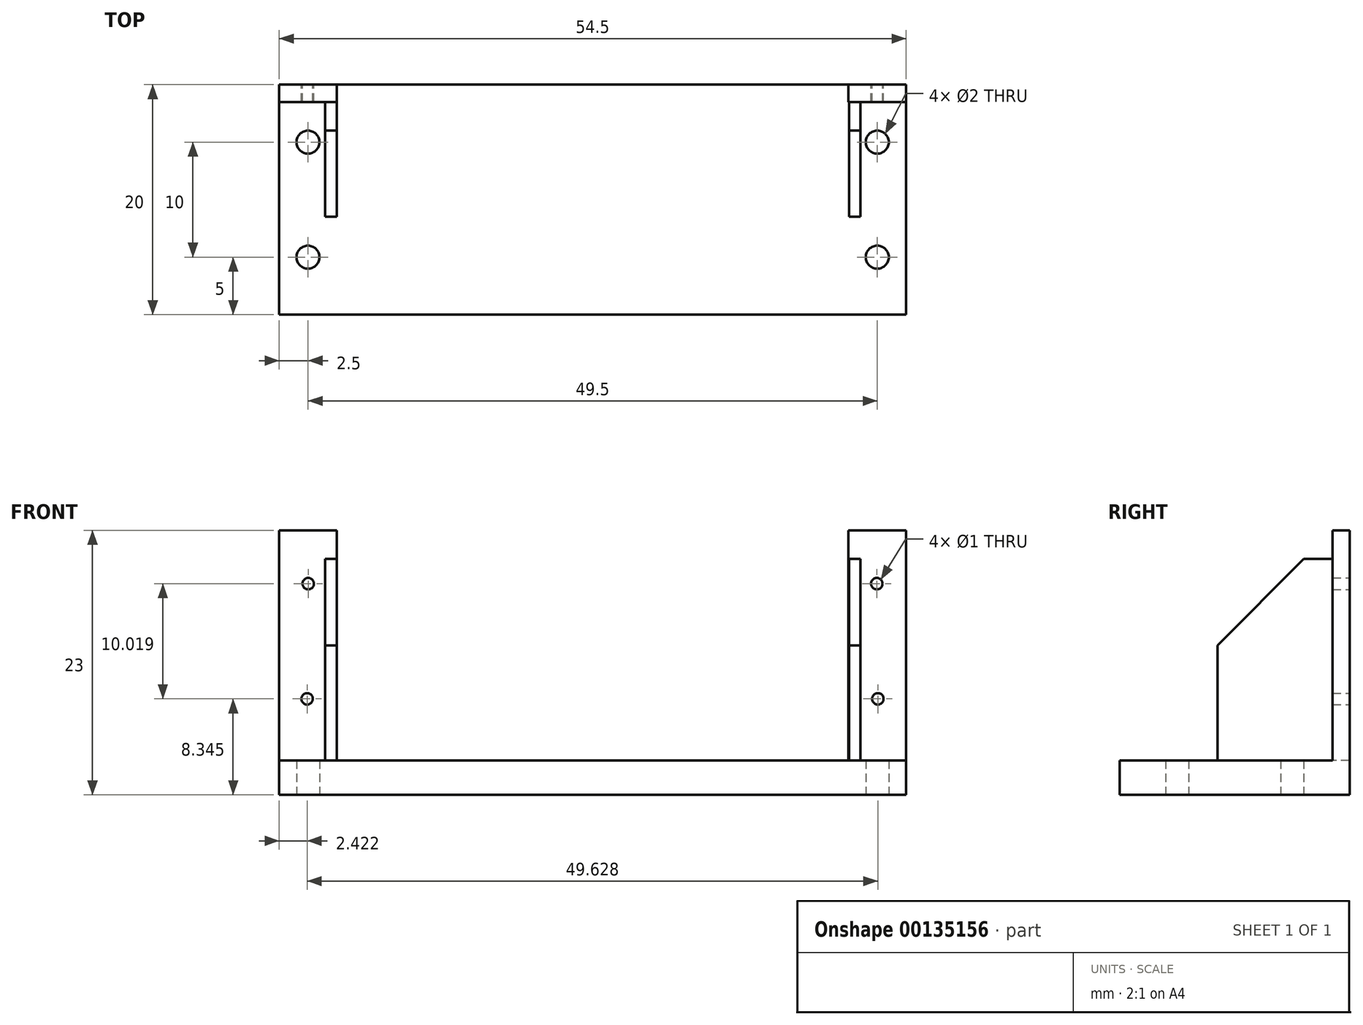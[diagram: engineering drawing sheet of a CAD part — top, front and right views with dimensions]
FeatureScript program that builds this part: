
annotation { "Feature Type Name" : "Feature", "Feature Type Description" : "" }
export const myFeature = defineFeature(function(context is Context, id is Id, definition is map)
    precondition{}
    {
        {
            var Q0;
            Q0=qCreatedBy(makeId("Top.planeOp"),FACE);
            var sketch = newSketch(context, id + "F0", { "sketchPlane" : qUnion([Q0])});
            skLineSegment(sketch, "E0.bottom", {"start": v(24.75, 5) * mm, "end": v(-24.75, 5) * mm, "construction": true});
            skLineSegment(sketch, "E0.top", {"start": v(24.75, -5) * mm, "end": v(-24.75, -5) * mm, "construction": true});
            skLineSegment(sketch, "E0.left", {"start": v(24.75, 5) * mm, "end": v(24.75, -5) * mm, "construction": true});
            skLineSegment(sketch, "E0.right", {"start": v(-24.75, 5) * mm, "end": v(-24.75, -5) * mm, "construction": true});
            skPoint(sketch, "E0.middle", {"position": v(0, 0) * mm});
            skLineSegment(sketch, "E1.bottom", {"start": v(27.25, 10) * mm, "end": v(-27.25, 10) * mm});
            skLineSegment(sketch, "E1.top", {"start": v(27.25, -10) * mm, "end": v(-27.25, -10) * mm});
            skLineSegment(sketch, "E1.left", {"start": v(27.25, 10) * mm, "end": v(27.25, -10) * mm});
            skLineSegment(sketch, "E1.right", {"start": v(-27.25, 10) * mm, "end": v(-27.25, -10) * mm});
            skCircle(sketch, "E2", {"center": v(-24.75, 5) * mm, "radius": 1 * mm});
            skCircle(sketch, "E3", {"center": v(24.75, 5) * mm, "radius": 1 * mm});
            skCircle(sketch, "E4", {"center": v(24.75, -5) * mm, "radius": 1 * mm});
            skCircle(sketch, "E5", {"center": v(-24.75, -5) * mm, "radius": 1 * mm});
            skSolve(sketch);
        }
        {
            var Q0;
            Q0=makeQuery(id+"F0.imprint","IMPRINT",FACE,{"disambiguationData":[TD([[makeQuery(id+"F0.imprint","IMPRINT",EDGE,{"derivedFrom":sQuery(id+"F0.wireOp",EDGE,"E1.bottom")}),1.0]])]});
            extrude(context, id + "F1", {"entities" : qUnion([Q0]), "depth" : 3 * mm});
        }
        {
            var Q0;
            Q0=makeQuery(id+"F1.opExtrude","CAP_FACE",FACE,{"disambiguationData":[OSD([sQuery(id+"F0.wireOp",EDGE,"E1.bottom"),sQuery(id+"F0.wireOp",EDGE,"E1.top"),sQuery(id+"F0.wireOp",EDGE,"E1.left"),sQuery(id+"F0.wireOp",EDGE,"E1.right"),sQuery(id+"F0.wireOp",EDGE,"E2"),sQuery(id+"F0.wireOp",EDGE,"E3"),sQuery(id+"F0.wireOp",EDGE,"E4"),sQuery(id+"F0.wireOp",EDGE,"E5")])],"isStart":false});
            var sketch = newSketch(context, id + "F2", { "sketchPlane" : qUnion([Q0])});
            skLineSegment(sketch, "E6.bottom", {"start": v(-27.25, 10) * mm, "end": v(-22.25, 10) * mm});
            skLineSegment(sketch, "E6.top", {"start": v(-27.25, 8.5) * mm, "end": v(-22.25, 8.5) * mm});
            skLineSegment(sketch, "E6.left", {"start": v(-27.25, 10) * mm, "end": v(-27.25, 8.5) * mm});
            skLineSegment(sketch, "E6.right", {"start": v(-22.25, 10) * mm, "end": v(-22.25, 8.5) * mm});
            skLineSegment(sketch, "E7.bottom", {"start": v(27.25, 10) * mm, "end": v(22.25, 10) * mm});
            skLineSegment(sketch, "E7.top", {"start": v(27.25, 8.5) * mm, "end": v(22.25, 8.5) * mm});
            skLineSegment(sketch, "E7.left", {"start": v(27.25, 10) * mm, "end": v(27.25, 8.5) * mm});
            skLineSegment(sketch, "E7.right", {"start": v(22.25, 10) * mm, "end": v(22.25, 8.5) * mm});
            skPoint(sketch, "E8", {"position": v(-22.25, 8.5) * mm});
            skPoint(sketch, "E9", {"position": v(22.25, 8.5) * mm});
            skSolve(sketch);
        }
        {
            var Q0;
            Q0=makeQuery(id+"F2.imprint","IMPRINT",FACE,{"disambiguationData":[TD([[makeQuery(id+"F2.imprint","IMPRINT",EDGE,{"derivedFrom":sQuery(id+"F2.wireOp",EDGE,"E6.bottom")}),1.0]])]});
            var Q1;
            Q1=makeQuery(id+"F2.imprint","IMPRINT",FACE,{"disambiguationData":[TD([[makeQuery(id+"F2.imprint","IMPRINT",EDGE,{"derivedFrom":sQuery(id+"F2.wireOp",EDGE,"E7.bottom")}),1.0]])]});
            var Q2;
            Q2=makeQuery(id+"F2.imprint","IMPRINT",FACE,{"disambiguationData":[TD([[makeQuery(id+"F2.imprint","IMPRINT",EDGE,{"derivedFrom":sQuery(id+"F2.wireOp",EDGE,"qa5opf6L-vfva-f9ps-wdat-dUW7fVkKqp9T.bottom")}),-1.0]])]});
            var Q3;
            Q3=makeQuery(id+"F2.imprint","IMPRINT",FACE,{"disambiguationData":[TD([[makeQuery(id+"F2.imprint","IMPRINT",EDGE,{"derivedFrom":sQuery(id+"F2.wireOp",EDGE,"lnxaC5Hq-gqwb-D7rE-EtE1-ObI2EhhsYE1f.bottom")}),-1.0]])]});
            extrude(context, id + "F3", {"entities" : qUnion([Q0, Q1, Q2, Q3]), "operationType" : NewBodyOperationType.ADD, "depth" : 20 * mm});
        }
        {
            var Q0;
            Q0=makeQuery(id+"F1.opExtrude","CAP_FACE",FACE,{"disambiguationData":[OSD([sQuery(id+"F0.wireOp",EDGE,"E1.bottom"),sQuery(id+"F0.wireOp",EDGE,"E1.top"),sQuery(id+"F0.wireOp",EDGE,"E1.left"),sQuery(id+"F0.wireOp",EDGE,"E1.right"),sQuery(id+"F0.wireOp",EDGE,"E2"),sQuery(id+"F0.wireOp",EDGE,"E3"),sQuery(id+"F0.wireOp",EDGE,"E4"),sQuery(id+"F0.wireOp",EDGE,"E5")])],"isStart":false});
            var sketch = newSketch(context, id + "F4", { "sketchPlane" : qUnion([Q0])});
            skLineSegment(sketch, "E10.bottom", {"start": v(-22.25, 8.5) * mm, "end": v(-23.25, 8.5) * mm});
            skLineSegment(sketch, "E10.top", {"start": v(-22.25, -1.5) * mm, "end": v(-23.25, -1.5) * mm});
            skLineSegment(sketch, "E10.left", {"start": v(-22.25, 8.5) * mm, "end": v(-22.25, -1.5) * mm});
            skLineSegment(sketch, "E10.right", {"start": v(-23.25, 8.5) * mm, "end": v(-23.25, -1.5) * mm});
            skLineSegment(sketch, "E11.bottom", {"start": v(22.29, 8.5) * mm, "end": v(23.29, 8.5) * mm});
            skLineSegment(sketch, "E11.top", {"start": v(22.29, -1.5) * mm, "end": v(23.29, -1.5) * mm});
            skLineSegment(sketch, "E11.left", {"start": v(22.29, 8.5) * mm, "end": v(22.29, -1.5) * mm});
            skLineSegment(sketch, "E11.right", {"start": v(23.29, 8.5) * mm, "end": v(23.29, -1.5) * mm});
            skSolve(sketch);
        }
        {
            var Q0;
            Q0 = qSketchRegion(id + "F4", true);
            extrude(context, id + "F5", {"entities" : qUnion([Q0]), "operationType" : NewBodyOperationType.ADD, "depth" : 17.5 * mm});
        }
        {
            var Q0;
            Q0=makeQuery(id+"F5.opExtrude","CAP_EDGE",EDGE,{"disambiguationData":[OSD([sQuery(id+"F4.wireOp",EDGE,"E10.top")])],"isStart":false});
            var Q1;
            Q1=makeQuery(id+"F5.opExtrude","CAP_EDGE",EDGE,{"disambiguationData":[OSD([sQuery(id+"F4.wireOp",EDGE,"E11.top")])],"isStart":false});
            chamfer(context, id + "F6", {"entities" : qUnion([Q0, Q1]), "width" : 7.5 * mm, "tangentPropagation" : true});
        }
        {
            var Q0;
            Q0=makeQuery(id+"F3.boolean.opBoolean","MERGE",FACE,{"derivedFrom":[makeQuery(id+"F1.opExtrude","SWEPT_FACE",FACE,{"disambiguationData":[OSD([sQuery(id+"F0.wireOp",EDGE,"E1.bottom")])]}),makeQuery(id+"F3.opExtrude","SWEPT_FACE",FACE,{"disambiguationData":[OSD([sQuery(id+"F2.wireOp",EDGE,"E6.bottom")])]}),makeQuery(id+"F3.opExtrude","SWEPT_FACE",FACE,{"disambiguationData":[OSD([sQuery(id+"F2.wireOp",EDGE,"E7.bottom")])]})]});
            var sketch = newSketch(context, id + "F7", { "sketchPlane" : qUnion([Q0])});
            skPoint(sketch, "E12", {"position": v(24.83, 8.34) * mm});
            skPoint(sketch, "E13", {"position": v(24.73, 18.36) * mm});
            skPoint(sketch, "E14", {"position": v(-24.8, 8.34) * mm});
            skPoint(sketch, "E15", {"position": v(-24.7, 18.36) * mm});
            skSolve(sketch);
        }
        {
            var Q0;
            Q0=sQuery(id+"F7.wireOp",VERTEX,"E12");
            var Q1;
            Q1=sQuery(id+"F7.wireOp",VERTEX,"E13");
            var Q2;
            Q2=sQuery(id+"F7.wireOp",VERTEX,"E14");
            var Q3;
            Q3=sQuery(id+"F7.wireOp",VERTEX,"E15");
            var Q4;
            Q4=makeQuery(id+"F1.opExtrude","SWEPT_BODY",BODY,{"disambiguationData":[OSD([sQuery(id+"F0.wireOp",EDGE,"E1.bottom"),sQuery(id+"F0.wireOp",EDGE,"E1.top"),sQuery(id+"F0.wireOp",EDGE,"E1.left"),sQuery(id+"F0.wireOp",EDGE,"E1.right"),sQuery(id+"F0.wireOp",EDGE,"E2"),sQuery(id+"F0.wireOp",EDGE,"E3"),sQuery(id+"F0.wireOp",EDGE,"E4"),sQuery(id+"F0.wireOp",EDGE,"E5")])]});
            hole(context, id + "F8", {"style" : HoleStyle.SIMPLE, "endStyle" : HoleEndStyle.THROUGH, "holeDiameter" : 1 * mm, "locations" : qUnion([Q0, Q1, Q2, Q3]), "scope" : qUnion([Q4]), "isTappedThrough" : true});
        }
    });
